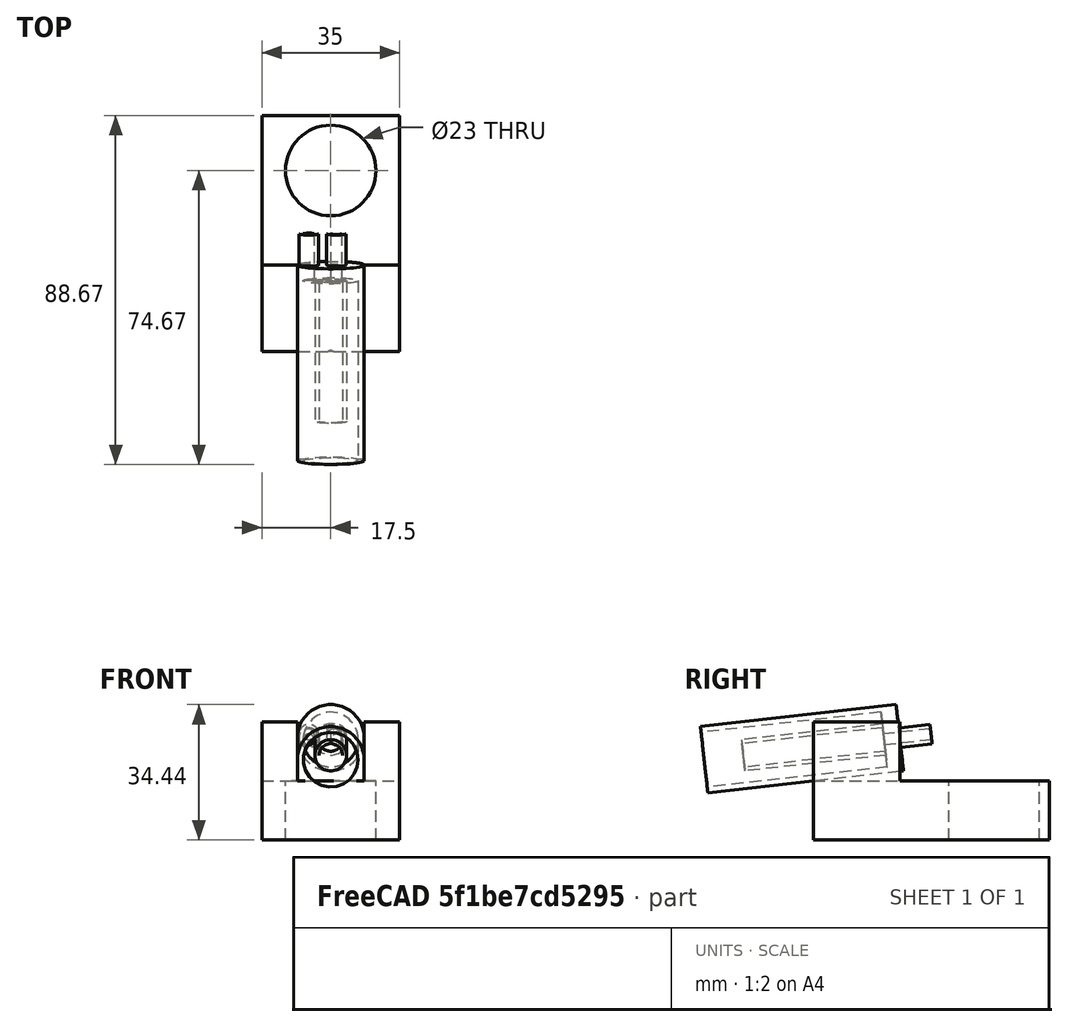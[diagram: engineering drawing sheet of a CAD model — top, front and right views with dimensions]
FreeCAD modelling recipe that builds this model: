
FCSTD DOCUMENT  (FreeCAD 0.18R16093 +53 (Git))
Label: isoflurane_mask_mouse_7
License: All rights reserved
LicenseURL: http://en.wikipedia.org/wiki/All_rights_reserved
objects: Part::Cylinder×9, Part::Cut×5, Part::MultiFuse×5, Part::Box×3
note: 22 computed .brp shape members not serialized (recipe doc carries the construction recipe); baked Part::Feature solids carry a one-line shape summary decoded from their .brp

FEATURE [Part::Box] Box  label="Cube"
  AttacherType = Attacher::AttachEngine3D
  Height = 15
  Length = 35
  Width = 60
FEATURE [Part::Cylinder] Cylinder
  Angle = 360
  AttacherType = Attacher::AttachEngine3D
  Height = 50
  Placement = pos=(17.5,22,26) rot=(1,0,0;1.5708rad)
  Radius = 8.5
FEATURE [Part::Box] Box001  label="Cube001"
  AttacherType = Attacher::AttachEngine3D
  Height = 15
  Length = 9
  Placement = pos=(0,0,15) rot=(0,0,1;0rad)
  Width = 22
FEATURE [Part::Box] Box002  label="Cube002"
  AttacherType = Attacher::AttachEngine3D
  Height = 15
  Length = 9
  Placement = pos=(26,0,15) rot=(0,0,1;0rad)
  Width = 22
FEATURE [Part::Cylinder] Cylinder002
  Angle = 360
  AttacherType = Attacher::AttachEngine3D
  Height = 46
  Placement = pos=(17.5,18,26) rot=(1,0,0;1.5708rad)
  Radius = 7
FEATURE [Part::Cylinder] Cylinder005
  Angle = 360
  AttacherType = Attacher::AttachEngine3D
  Height = 60
  Placement = pos=(17.5,18,26) rot=(1,0,0;1.5708rad)
  Radius = 3
FEATURE [Part::Cylinder] Cylinder006
  Angle = 360
  AttacherType = Attacher::AttachEngine3D
  Height = 12
  Placement = pos=(18.9,30,26) rot=(1,0,0;1.5708rad)
  Radius = 2.5
FEATURE [Part::Cylinder] Cylinder007
  Angle = 360
  AttacherType = Attacher::AttachEngine3D
  Height = 50
  Placement = pos=(18.9,45,26) rot=(1,0,0;1.5708rad)
  Radius = 1.4
FEATURE [Part::Cylinder] Cylinder008
  Angle = 360
  AttacherType = Attacher::AttachEngine3D
  Height = 12
  Placement = pos=(11.9,30,26) rot=(1,0,0;1.5708rad)
  Radius = 2.5
FEATURE [Part::Cylinder] Cylinder009
  Angle = 360
  AttacherType = Attacher::AttachEngine3D
  Height = 50
  Placement = pos=(11.9,44,26) rot=(1,0,0;1.5708rad)
  Radius = 1.4
FEATURE [Part::Cylinder] Cylinder004
  Angle = 360
  AttacherType = Attacher::AttachEngine3D
  Height = 40
  Placement = pos=(17.5,22,26) rot=(1,0,0;1.5708rad)
  Radius = 4
FEATURE [Part::Cut] Cut001
  Base = -> Cylinder
  Tool = -> Cylinder002
FEATURE [Part::Cut] Cut002
  Base = -> Cylinder004
  Tool = -> Cylinder005
FEATURE [Part::MultiFuse] Fusion
  Shapes = -> [Cut001,Cut002]
FEATURE [Part::MultiFuse] Fusion001
  Shapes = -> [Fusion,Cylinder006]
FEATURE [Part::Cut] Cut003
  Base = -> Fusion001
  Tool = -> Cylinder007
FEATURE [Part::MultiFuse] Fusion002
  Shapes = -> [Cut003,Cylinder008]
FEATURE [Part::Cut] Cut004
  Base = -> Fusion002
  Placement = pos=(0,3,-2.3) rot=(1,0,0;0.111701rad)
  Tool = -> Cylinder009
FEATURE [Part::MultiFuse] Fusion003
  Shapes = -> [Cut004,Box002,Box001]
FEATURE [Part::Cylinder] Cylinder010
  Angle = 360
  AttacherType = Attacher::AttachEngine3D
  Height = 20
  Placement = pos=(17.5,46,-2) rot=(0,0,1;0rad)
  Radius = 11.5
FEATURE [Part::Cut] Cut
  Base = -> Box
  Tool = -> Cylinder010
FEATURE [Part::MultiFuse] Fusion004
  Shapes = -> [Fusion003,Cut]
